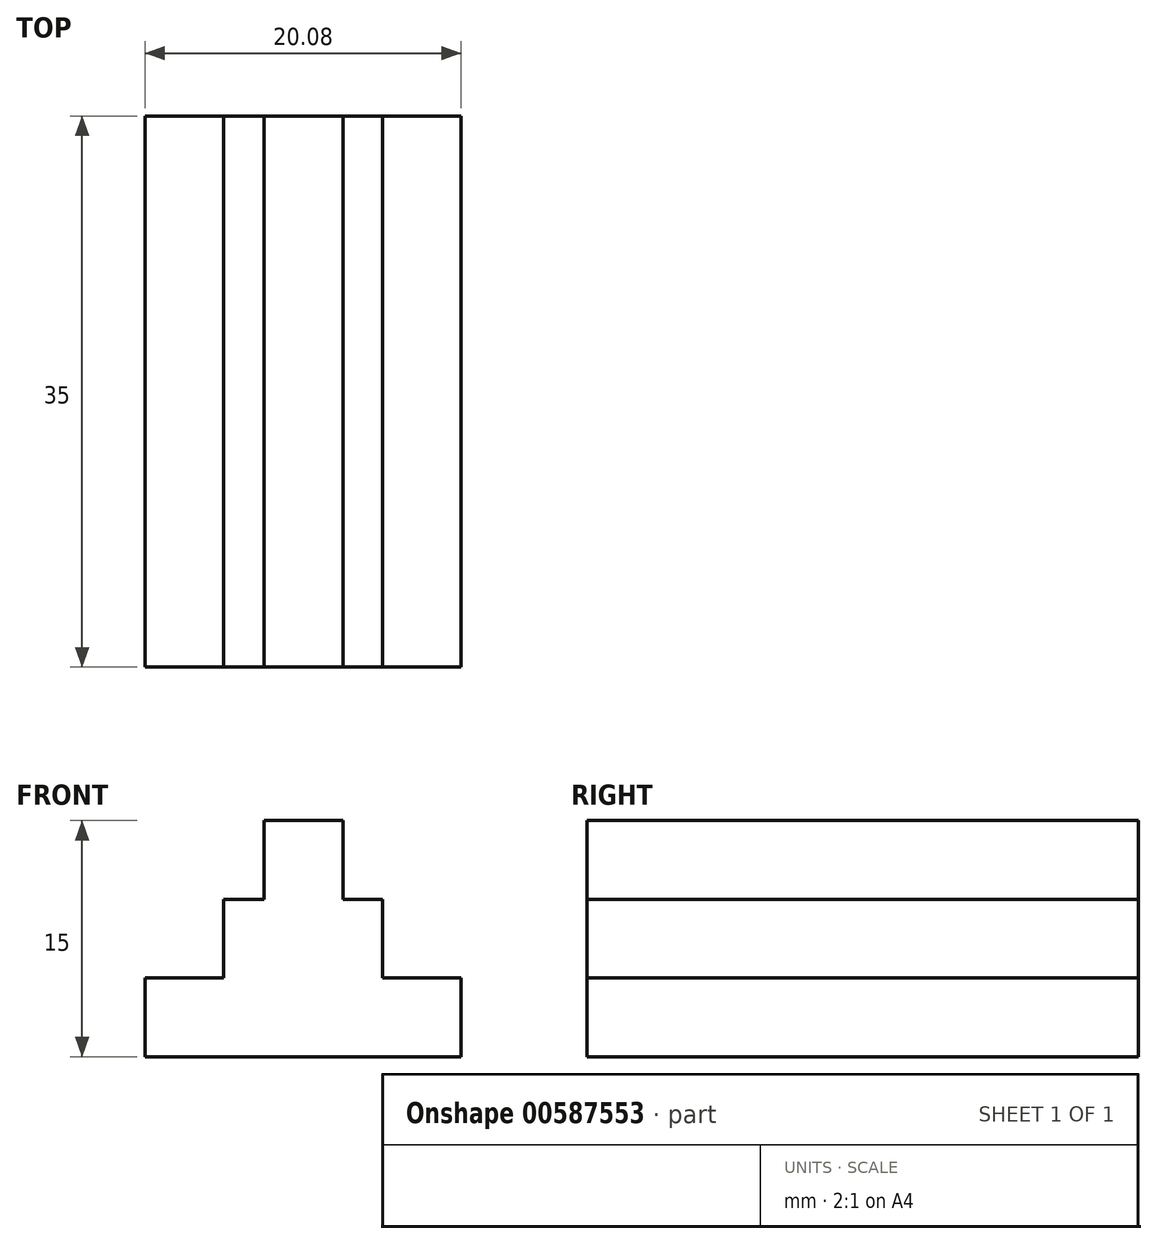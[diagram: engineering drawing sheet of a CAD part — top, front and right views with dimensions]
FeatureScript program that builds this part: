
annotation { "Feature Type Name" : "Feature", "Feature Type Description" : "" }
export const myFeature = defineFeature(function(context is Context, id is Id, definition is map)
    precondition{}
    {
        {
            var Q0;
            Q0=qCreatedBy(makeId("Front.planeOp"),FACE);
            var sketch = newSketch(context, id + "F0", { "sketchPlane" : qUnion([Q0])});
            skLineSegment(sketch, "E0", {"start": v(-5, 15.9) * mm, "end": v(0, 15.9) * mm});
            skLineSegment(sketch, "E1", {"start": v(-2.5, 15.9) * mm, "end": v(-2.5, 10.9) * mm});
            skLineSegment(sketch, "E2", {"start": v(-2.5, 15.9) * mm, "end": v(-5, 15.9) * mm});
            skLineSegment(sketch, "E3", {"start": v(-5, 15.9) * mm, "end": v(-5, 10.9) * mm});
            skLineSegment(sketch, "E4", {"start": v(-5, 10.9) * mm, "end": v(-2.5, 10.9) * mm});
            skLineSegment(sketch, "E5", {"start": v(0, 15.9) * mm, "end": v(0, 10.9) * mm});
            skLineSegment(sketch, "E6", {"start": v(0, 10.9) * mm, "end": v(-2.5, 10.9) * mm});
            skLineSegment(sketch, "E7", {"start": v(-7.58, 10.9) * mm, "end": v(-5, 10.9) * mm});
            skLineSegment(sketch, "E8", {"start": v(2.5, 10.9) * mm, "end": v(0, 10.9) * mm});
            skLineSegment(sketch, "E9", {"start": v(-7.58, 10.9) * mm, "end": v(-7.58, 5.9) * mm});
            skLineSegment(sketch, "E10", {"start": v(2.5, 10.9) * mm, "end": v(2.5, 5.9) * mm});
            skLineSegment(sketch, "E11", {"start": v(-7.58, 5.9) * mm, "end": v(-12.58, 5.9) * mm});
            skLineSegment(sketch, "E12", {"start": v(-12.58, 5.9) * mm, "end": v(-12.58, 0.9) * mm});
            skLineSegment(sketch, "E13", {"start": v(2.5, 5.9) * mm, "end": v(7.5, 5.9) * mm});
            skLineSegment(sketch, "E14", {"start": v(7.5, 5.9) * mm, "end": v(7.5, 0.9) * mm});
            skLineSegment(sketch, "E15", {"start": v(-12.58, 0.9) * mm, "end": v(7.5, 0.9) * mm});
            skPoint(sketch, "E16.orphan", {"position": v(-27.5, 15.9) * mm});
            skPoint(sketch, "E17.start.orphan", {"position": v(22.5, 15.9) * mm});
            skSolve(sketch);
        }
        {
            var Q0;
            Q0 = qSketchRegion(id + "F0", true);
            extrude(context, id + "F1", {"entities" : qUnion([Q0]), "depth" : 35 * mm, "offsetDistance" : 25 * mm});
        }
    });
